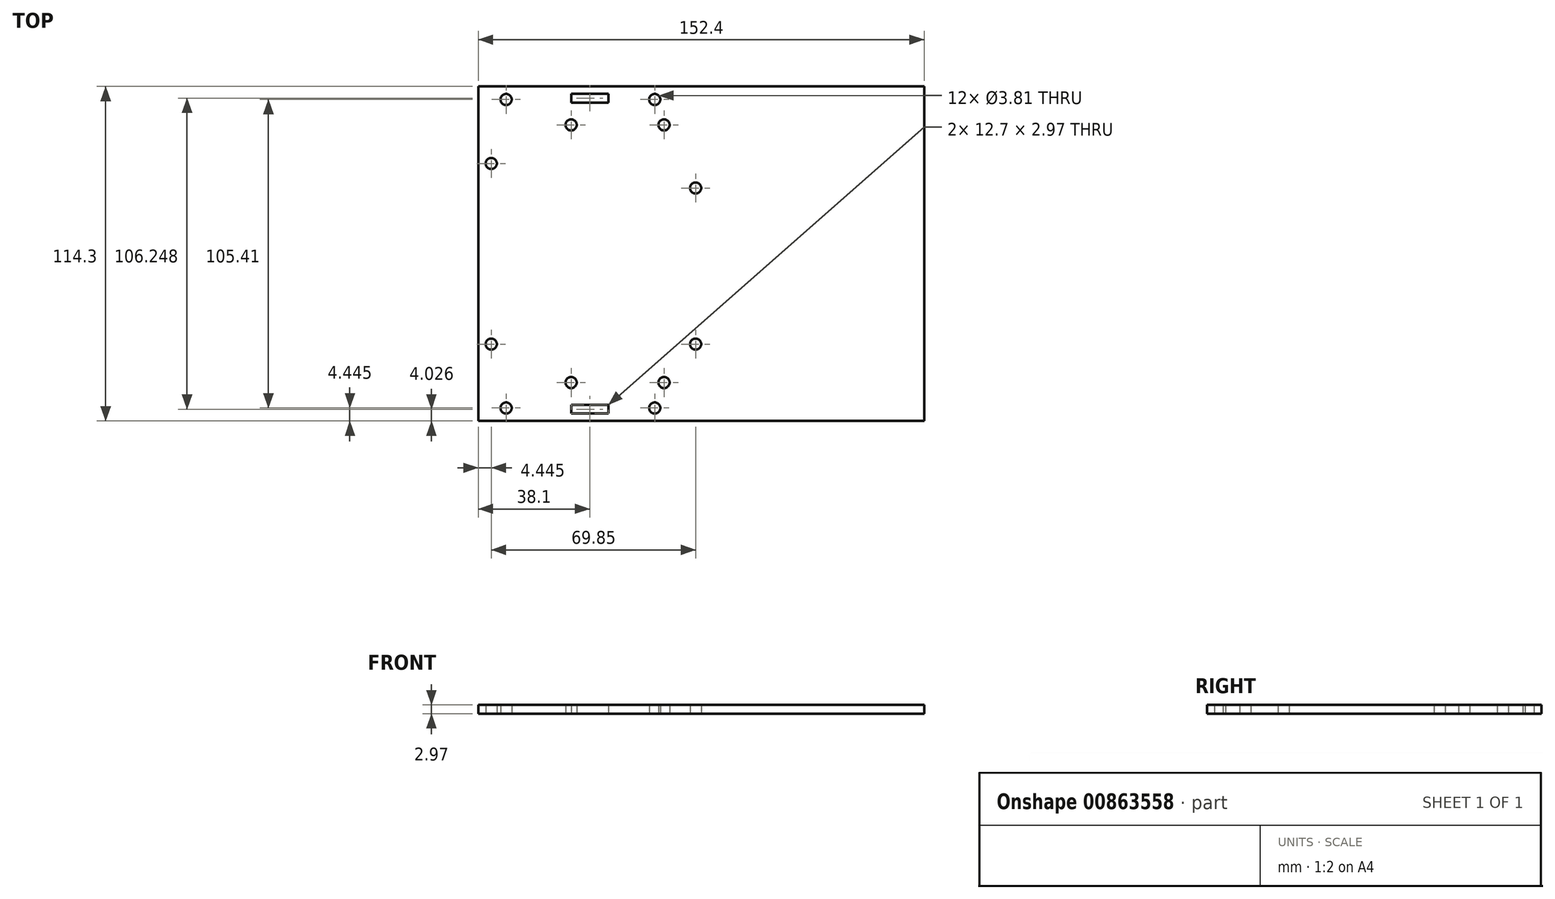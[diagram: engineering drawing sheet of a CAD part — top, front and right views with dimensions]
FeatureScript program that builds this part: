
annotation { "Feature Type Name" : "Feature", "Feature Type Description" : "" }
export const myFeature = defineFeature(function(context is Context, id is Id, definition is map)
    precondition{}
    {
        {
            var Q0;
            Q0=qCreatedBy(makeId("Top.planeOp"),FACE);
            var sketch = newSketch(context, id + "F0", { "sketchPlane" : qUnion([Q0])});
            skLineSegment(sketch, "E0.bottom", {"start": v(-63.5, -57.15) * mm, "end": v(88.9, -57.15) * mm});
            skLineSegment(sketch, "E0.top", {"start": v(-63.5, 57.15) * mm, "end": v(88.9, 57.15) * mm});
            skLineSegment(sketch, "E0.left", {"start": v(-63.5, -57.15) * mm, "end": v(-63.5, 57.15) * mm});
            skLineSegment(sketch, "E0.right", {"start": v(88.9, -57.15) * mm, "end": v(88.9, 57.15) * mm});
            skCircle(sketch, "E1", {"center": v(-53.98, 52.7) * mm, "radius": 1.9 * mm});
            skCircle(sketch, "E2", {"center": v(-3.17, 52.7) * mm, "radius": 1.9 * mm});
            skCircle(sketch, "E3", {"center": v(-53.97, -52.7) * mm, "radius": 1.9 * mm});
            skCircle(sketch, "E4", {"center": v(-3.17, -52.7) * mm, "radius": 1.9 * mm});
            skLineSegment(sketch, "E5.bottom", {"start": v(-31.75, 51.64) * mm, "end": v(-19.05, 51.64) * mm});
            skLineSegment(sketch, "E5.top", {"start": v(-31.75, 54.61) * mm, "end": v(-19.05, 54.61) * mm});
            skLineSegment(sketch, "E5.left", {"start": v(-31.75, 51.64) * mm, "end": v(-31.75, 54.61) * mm});
            skLineSegment(sketch, "E5.right", {"start": v(-19.05, 51.64) * mm, "end": v(-19.05, 54.61) * mm});
            skLineSegment(sketch, "E6.bottom", {"start": v(-31.75, -54.6) * mm, "end": v(-19.05, -54.6) * mm});
            skLineSegment(sketch, "E6.top", {"start": v(-31.75, -51.64) * mm, "end": v(-19.05, -51.64) * mm});
            skLineSegment(sketch, "E6.left", {"start": v(-31.75, -54.61) * mm, "end": v(-31.75, -51.64) * mm});
            skLineSegment(sketch, "E6.right", {"start": v(-19.05, -54.61) * mm, "end": v(-19.05, -51.64) * mm});
            skCircle(sketch, "E7", {"center": v(-59.05, -30.89) * mm, "radius": 1.9 * mm});
            skCircle(sketch, "E8", {"center": v(-59.06, 30.84) * mm, "radius": 1.9 * mm});
            skCircle(sketch, "E9", {"center": v(10.8, 22.45) * mm, "radius": 1.9 * mm});
            skCircle(sketch, "E10", {"center": v(10.8, -30.89) * mm, "radius": 1.9 * mm});
            skCircle(sketch, "E11", {"center": v(-31.75, 44.02) * mm, "radius": 1.9 * mm});
            skCircle(sketch, "E12", {"center": v(0, 44.02) * mm, "radius": 1.9 * mm});
            skCircle(sketch, "E13", {"center": v(0, -44.02) * mm, "radius": 1.9 * mm});
            skCircle(sketch, "E14", {"center": v(-31.75, -44.02) * mm, "radius": 1.9 * mm});
            skSolve(sketch);
        }
        {
            var Q0;
            Q0 = qSketchRegion(id + "F0", true);
            extrude(context, id + "F1", {"entities" : qUnion([Q0]), "depth" : 2.97 * mm, "offsetDistance" : 25.4 * mm});
        }
    });
